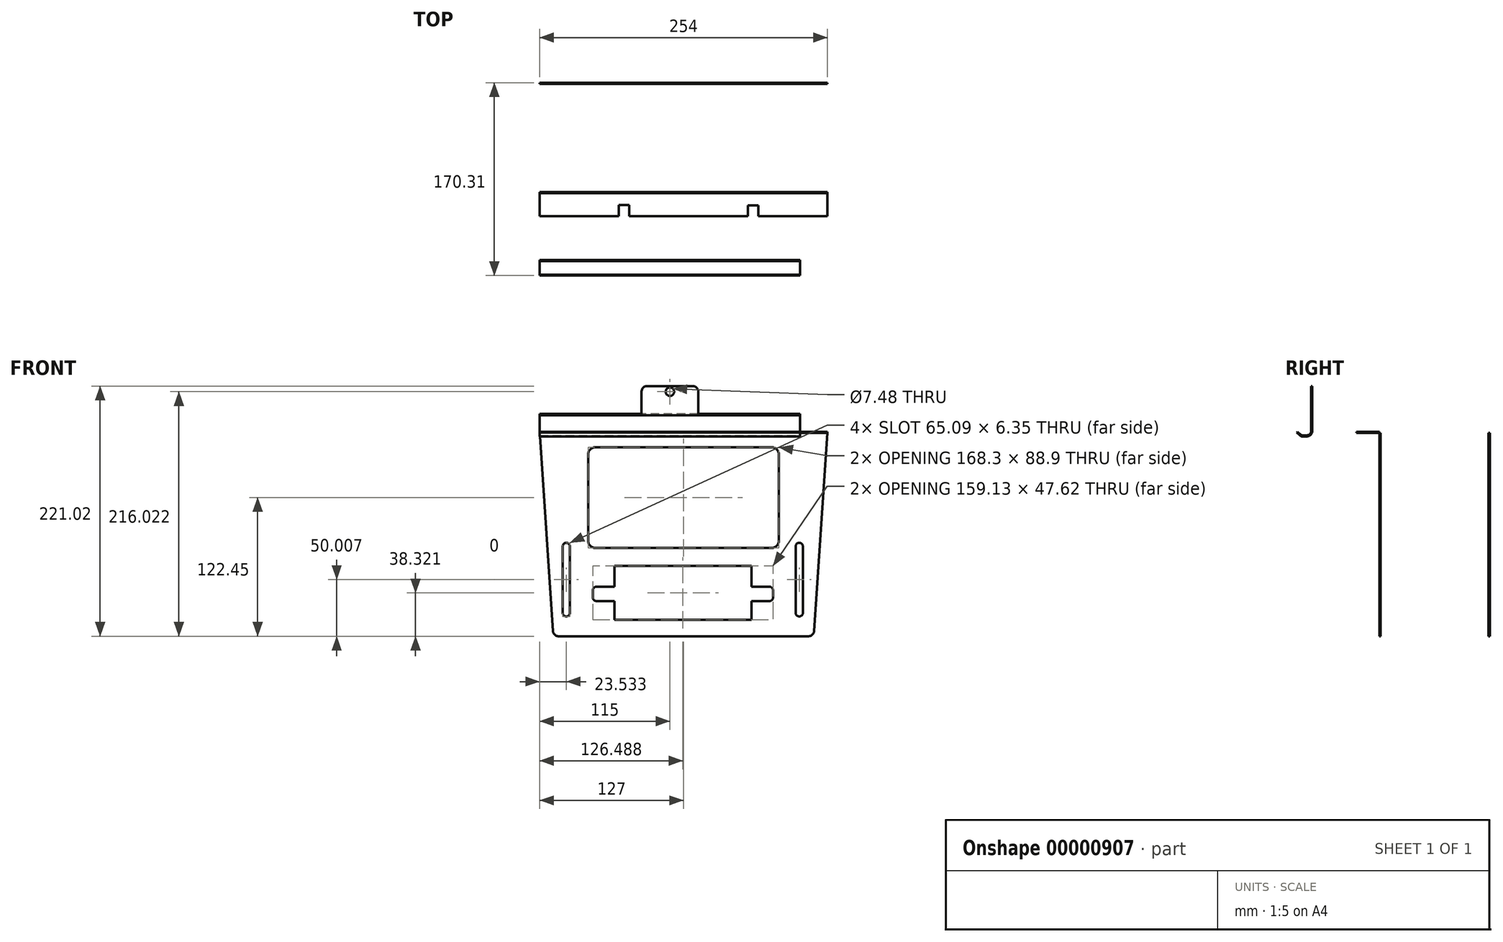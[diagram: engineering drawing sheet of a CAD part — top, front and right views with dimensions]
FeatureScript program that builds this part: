
annotation { "Feature Type Name" : "Feature", "Feature Type Description" : "" }
export const myFeature = defineFeature(function(context is Context, id is Id, definition is map)
    precondition{}
    {
        {
            var Q0;
            Q0=qCreatedBy(makeId("Top.planeOp"),FACE);
            var sketch = newSketch(context, id + "F0", { "sketchPlane" : qUnion([Q0])});
            skLineSegment(sketch, "E0", {"start": v(0, 0) * mm, "end": v(254, 0) * mm});
            skLineSegment(sketch, "E1", {"start": v(254, 0) * mm, "end": v(254, 20.25) * mm});
            skLineSegment(sketch, "E2", {"start": v(254, 20.25) * mm, "end": v(0, 20.25) * mm});
            skLineSegment(sketch, "E3", {"start": v(0, 20.25) * mm, "end": v(0, 0) * mm});
            skLineSegment(sketch, "E4.bottom", {"start": v(70, 20.25) * mm, "end": v(79, 20.25) * mm});
            skLineSegment(sketch, "E4.top", {"start": v(70, 10.6) * mm, "end": v(79, 10.6) * mm});
            skLineSegment(sketch, "E4.left", {"start": v(70, 20.25) * mm, "end": v(70, 10.6) * mm});
            skLineSegment(sketch, "E4.right", {"start": v(79, 20.25) * mm, "end": v(79, 10.6) * mm});
            skLineSegment(sketch, "E5.bottom", {"start": v(184, 20.25) * mm, "end": v(193, 20.25) * mm});
            skLineSegment(sketch, "E5.top", {"start": v(184, 10.9) * mm, "end": v(193, 10.9) * mm});
            skLineSegment(sketch, "E5.left", {"start": v(193, 20.25) * mm, "end": v(193, 10.9) * mm});
            skLineSegment(sketch, "E5.right", {"start": v(184, 20.25) * mm, "end": v(184, 10.9) * mm});
            skSolve(sketch);
        }
        {
            var Q0;
            Q0=qCreatedBy(makeId("Front.planeOp"),FACE);
            var sketch = newSketch(context, id + "F1", { "sketchPlane" : qUnion([Q0])});
            skLineSegment(sketch, "E6", {"start": v(0, 0) * mm, "end": v(11.69, 174.93) * mm});
            skLineSegment(sketch, "E7", {"start": v(16.68, 179.6) * mm, "end": v(237.32, 179.6) * mm});
            skLineSegment(sketch, "E8", {"start": v(242.31, 174.93) * mm, "end": v(254, 0) * mm});
            skLineSegment(sketch, "E9", {"start": v(254, 0) * mm, "end": v(0, 0) * mm});
            skPoint(sketch, "E10.visualSharp", {"position": v(12, 179.6) * mm});
            skArc(sketch, "E10.filletArc", {"start": v(16.68, 179.6) * mm, "mid": v(13.26, 178.25) * mm, "end": v(11.69, 174.93) * mm});
            skPoint(sketch, "E11.visualSharp", {"position": v(242, 179.6) * mm});
            skArc(sketch, "E11.filletArc", {"start": v(242.31, 174.93) * mm, "mid": v(240.74, 178.25) * mm, "end": v(237.32, 179.6) * mm});
            skLineSegment(sketch, "E12", {"start": v(16.68, 179.6) * mm, "end": v(16.68, 199.6) * mm});
            skLineSegment(sketch, "E13", {"start": v(16.68, 199.6) * mm, "end": v(236.05, 199.6) * mm});
            skLineSegment(sketch, "E14", {"start": v(236.05, 199.6) * mm, "end": v(237.32, 179.6) * mm});
            skLineSegment(sketch, "E15.bottom", {"start": v(49.2, 101.6) * mm, "end": v(204.8, 101.6) * mm});
            skLineSegment(sketch, "E15.top", {"start": v(49.2, 12.7) * mm, "end": v(204.8, 12.7) * mm});
            skLineSegment(sketch, "E15.left", {"start": v(42.85, 95.25) * mm, "end": v(42.85, 19.05) * mm});
            skLineSegment(sketch, "E15.right", {"start": v(211.15, 95.25) * mm, "end": v(211.15, 19.05) * mm});
            skPoint(sketch, "E16.visualSharp", {"position": v(42.85, 101.6) * mm});
            skArc(sketch, "E16.filletArc", {"start": v(49.2, 101.6) * mm, "mid": v(44.7, 99.74) * mm, "end": v(42.85, 95.25) * mm});
            skPoint(sketch, "E17.visualSharp", {"position": v(211.15, 101.6) * mm});
            skArc(sketch, "E17.filletArc", {"start": v(211.15, 95.25) * mm, "mid": v(209.3, 99.74) * mm, "end": v(204.8, 101.6) * mm});
            skPoint(sketch, "E18.visualSharp", {"position": v(211.15, 12.7) * mm});
            skArc(sketch, "E18.filletArc", {"start": v(204.8, 12.7) * mm, "mid": v(209.3, 14.56) * mm, "end": v(211.15, 19.05) * mm});
            skPoint(sketch, "E19.visualSharp", {"position": v(42.85, 12.7) * mm});
            skArc(sketch, "E19.filletArc", {"start": v(42.85, 19.05) * mm, "mid": v(44.7, 14.56) * mm, "end": v(49.2, 12.7) * mm});
            skLineSegment(sketch, "E20.bottom", {"start": v(65.97, 165.1) * mm, "end": v(187, 165.1) * mm});
            skLineSegment(sketch, "E20.top", {"start": v(65.97, 117.47) * mm, "end": v(187, 117.47) * mm});
            skLineSegment(sketch, "E21.bottom", {"start": v(23.53, 162.14) * mm, "end": v(23.53, 162.14) * mm});
            skLineSegment(sketch, "E21.top", {"start": v(23.53, 97.05) * mm, "end": v(23.53, 97.05) * mm});
            skLineSegment(sketch, "E21.left", {"start": v(26.7, 158.96) * mm, "end": v(26.7, 100.22) * mm});
            skLineSegment(sketch, "E21.right", {"start": v(20.36, 158.96) * mm, "end": v(20.36, 100.22) * mm});
            skPoint(sketch, "E22.visualSharp", {"position": v(26.7, 162.14) * mm});
            skArc(sketch, "E22.filletArc", {"start": v(26.7, 158.96) * mm, "mid": v(25.78, 161.2) * mm, "end": v(23.53, 162.14) * mm});
            skPoint(sketch, "E23.visualSharp", {"position": v(26.7, 97.05) * mm});
            skArc(sketch, "E23.filletArc", {"start": v(23.53, 97.05) * mm, "mid": v(25.78, 97.98) * mm, "end": v(26.7, 100.22) * mm});
            skPoint(sketch, "E24.visualSharp", {"position": v(20.36, 97.05) * mm});
            skArc(sketch, "E24.filletArc", {"start": v(20.36, 100.22) * mm, "mid": v(21.29, 97.98) * mm, "end": v(23.53, 97.05) * mm});
            skPoint(sketch, "E25.visualSharp", {"position": v(20.36, 162.14) * mm});
            skArc(sketch, "E25.filletArc", {"start": v(23.53, 162.14) * mm, "mid": v(21.29, 161.2) * mm, "end": v(20.36, 158.96) * mm});
            skArc(sketch, "E26.0.MirrorCS", {"start": v(229.2, 97.05) * mm, "mid": v(226.95, 97.98) * mm, "end": v(226.02, 100.22) * mm});
            skArc(sketch, "E26.1.MirrorCS", {"start": v(226.02, 158.96) * mm, "mid": v(226.95, 161.2) * mm, "end": v(229.2, 162.14) * mm});
            skPoint(sketch, "E26.2.MirrorP", {"position": v(232.37, 97.05) * mm});
            skLineSegment(sketch, "E26.3.MirrorCS", {"start": v(226.02, 158.96) * mm, "end": v(226.02, 100.22) * mm});
            skPoint(sketch, "E26.4.MirrorP", {"position": v(226.02, 97.05) * mm});
            skArc(sketch, "E26.5.MirrorCS", {"start": v(229.2, 162.14) * mm, "mid": v(231.44, 161.2) * mm, "end": v(232.37, 158.96) * mm});
            skLineSegment(sketch, "E26.6.MirrorCS", {"start": v(232.37, 158.96) * mm, "end": v(232.37, 100.22) * mm});
            skPoint(sketch, "E26.7.MirrorP", {"position": v(226.02, 162.14) * mm});
            skArc(sketch, "E26.9.MirrorCS", {"start": v(232.37, 100.22) * mm, "mid": v(231.44, 97.98) * mm, "end": v(229.2, 97.05) * mm});
            skPoint(sketch, "E26.10.MirrorP", {"position": v(232.37, 162.14) * mm});
            skLineSegment(sketch, "E27.bottom", {"start": v(65.97, 148.57) * mm, "end": v(50.1, 148.57) * mm});
            skLineSegment(sketch, "E27.top", {"start": v(65.97, 135.87) * mm, "end": v(50.1, 135.87) * mm});
            skLineSegment(sketch, "E27.right", {"start": v(46.92, 145.4) * mm, "end": v(46.92, 139.04) * mm});
            skLineSegment(sketch, "E28", {"start": v(65.97, 165.1) * mm, "end": v(65.97, 148.57) * mm});
            skLineSegment(sketch, "E29", {"start": v(65.97, 135.87) * mm, "end": v(65.97, 117.47) * mm});
            skPoint(sketch, "E30.visualSharp", {"position": v(46.92, 148.57) * mm});
            skArc(sketch, "E30.filletArc", {"start": v(50.1, 148.57) * mm, "mid": v(47.85, 147.64) * mm, "end": v(46.92, 145.4) * mm});
            skPoint(sketch, "E31.visualSharp", {"position": v(46.92, 135.87) * mm});
            skArc(sketch, "E31.filletArc", {"start": v(46.92, 139.04) * mm, "mid": v(47.85, 136.8) * mm, "end": v(50.1, 135.87) * mm});
            skArc(sketch, "E32.0.MirrorCS", {"start": v(202.88, 148.57) * mm, "mid": v(205.12, 147.64) * mm, "end": v(206.05, 145.4) * mm});
            skLineSegment(sketch, "E32.1.MirrorCS", {"start": v(206.05, 145.4) * mm, "end": v(206.05, 139.04) * mm});
            skArc(sketch, "E32.2.MirrorCS", {"start": v(206.05, 139.04) * mm, "mid": v(205.12, 136.8) * mm, "end": v(202.88, 135.87) * mm});
            skPoint(sketch, "E32.3.MirrorP", {"position": v(206.05, 135.87) * mm});
            skPoint(sketch, "E32.4.MirrorP", {"position": v(206.05, 148.57) * mm});
            skLineSegment(sketch, "E33.0.MirrorCS", {"start": v(187, 148.57) * mm, "end": v(202.88, 148.57) * mm});
            skLineSegment(sketch, "E34.0.MirrorCS", {"start": v(187, 135.87) * mm, "end": v(202.88, 135.87) * mm});
            skLineSegment(sketch, "E35", {"start": v(187, 148.57) * mm, "end": v(187, 165.1) * mm});
            skLineSegment(sketch, "E36", {"start": v(187, 135.87) * mm, "end": v(187, 117.47) * mm});
            skSolve(sketch);
        }
        {
            var Q0;
            Q0=makeQuery(id+"F1.imprint","IMPRINT",FACE,{"disambiguationData":[TD([[makeQuery(id+"F1.imprint","IMPRINT",EDGE,{"derivedFrom":sQuery(id+"F1.wireOp",EDGE,"E6")}),-1.0]])]});
            extrude(context, id + "F2", {"entities" : qUnion([Q0]), "depth" : 1 * mm});
        }
        {
            var Q0;
            Q0=makeQuery(id+"F0.imprint","IMPRINT",FACE,{"disambiguationData":[TD([[makeQuery(id+"F0.imprint","IMPRINT",EDGE,{"derivedFrom":sQuery(id+"F0.wireOp",EDGE,"E0")}),1.0]])]});
            extrude(context, id + "F3", {"entities" : qUnion([Q0]), "operationType" : NewBodyOperationType.ADD, "oppositeDirection" : true, "depth" : 1 * mm});
        }
        {
            var Q0;
            Q0=makeQuery(id+"F2.opExtrude","SWEPT_BODY",BODY,{"disambiguationData":[OSD([sQuery(id+"F1.wireOp",EDGE,"E6"),sQuery(id+"F1.wireOp",EDGE,"E7"),sQuery(id+"F1.wireOp",EDGE,"E8"),sQuery(id+"F1.wireOp",EDGE,"E9"),sQuery(id+"F1.wireOp",EDGE,"E10.filletArc"),sQuery(id+"F1.wireOp",EDGE,"E11.filletArc"),sQuery(id+"F1.wireOp",EDGE,"E15.bottom"),sQuery(id+"F1.wireOp",EDGE,"E15.top"),sQuery(id+"F1.wireOp",EDGE,"E15.left"),sQuery(id+"F1.wireOp",EDGE,"E15.right"),sQuery(id+"F1.wireOp",EDGE,"E16.filletArc"),sQuery(id+"F1.wireOp",EDGE,"E17.filletArc"),sQuery(id+"F1.wireOp",EDGE,"E18.filletArc"),sQuery(id+"F1.wireOp",EDGE,"E19.filletArc"),sQuery(id+"F1.wireOp",EDGE,"E20.bottom"),sQuery(id+"F1.wireOp",EDGE,"E20.top"),sQuery(id+"F1.wireOp",EDGE,"E21.left"),sQuery(id+"F1.wireOp",EDGE,"E21.right"),sQuery(id+"F1.wireOp",EDGE,"E22.filletArc"),sQuery(id+"F1.wireOp",EDGE,"E23.filletArc"),sQuery(id+"F1.wireOp",EDGE,"E24.filletArc"),sQuery(id+"F1.wireOp",EDGE,"E25.filletArc"),sQuery(id+"F1.wireOp",EDGE,"E26.0.MirrorCS"),sQuery(id+"F1.wireOp",EDGE,"E26.1.MirrorCS"),sQuery(id+"F1.wireOp",EDGE,"E26.3.MirrorCS"),sQuery(id+"F1.wireOp",EDGE,"E26.5.MirrorCS"),sQuery(id+"F1.wireOp",EDGE,"E26.6.MirrorCS"),sQuery(id+"F1.wireOp",EDGE,"E26.9.MirrorCS"),sQuery(id+"F1.wireOp",EDGE,"E27.bottom"),sQuery(id+"F1.wireOp",EDGE,"E27.top"),sQuery(id+"F1.wireOp",EDGE,"E27.right"),sQuery(id+"F1.wireOp",EDGE,"E28"),sQuery(id+"F1.wireOp",EDGE,"E29"),sQuery(id+"F1.wireOp",EDGE,"E30.filletArc"),sQuery(id+"F1.wireOp",EDGE,"E31.filletArc"),sQuery(id+"F1.wireOp",EDGE,"E32.0.MirrorCS"),sQuery(id+"F1.wireOp",EDGE,"E32.1.MirrorCS"),sQuery(id+"F1.wireOp",EDGE,"E32.2.MirrorCS"),sQuery(id+"F1.wireOp",EDGE,"E33.0.MirrorCS"),sQuery(id+"F1.wireOp",EDGE,"E34.0.MirrorCS"),sQuery(id+"F1.wireOp",EDGE,"E35"),sQuery(id+"F1.wireOp",EDGE,"E36")])]});
            var Q1;
            Q1=makeQuery(id+"F3.opExtrude","SWEPT_BODY",BODY,{"disambiguationData":[OSD([sQuery(id+"F0.wireOp",EDGE,"E0"),sQuery(id+"F0.wireOp",EDGE,"E1"),sQuery(id+"F0.wireOp",EDGE,"E2"),sQuery(id+"F0.wireOp",EDGE,"E3"),sQuery(id+"F0.wireOp",EDGE,"E4.top"),sQuery(id+"F0.wireOp",EDGE,"E4.left"),sQuery(id+"F0.wireOp",EDGE,"E4.right"),sQuery(id+"F0.wireOp",EDGE,"E5.top"),sQuery(id+"F0.wireOp",EDGE,"E5.left"),sQuery(id+"F0.wireOp",EDGE,"E5.right")])]});
            var Q2;
            Q2=makeQuery(id+"F2.opExtrude","CAP_EDGE",EDGE,{"disambiguationData":[OSD([sQuery(id+"F1.wireOp",EDGE,"E9")])],"isStart":false});
            transform(context, id + "F4", {"entities" : qUnion([Q0, Q1]), "transformType" : TransformType.ROTATION, "transformAxis" : qUnion([Q2]), "angle" : 180 * degree, "oppositeX" : false, "oppositeY" : false, "oppositeZ" : false, "makeCopy" : false});
        }
        {
            var Q0;
            Q0=qCreatedBy(makeId("Right.planeOp"),FACE);
            var sketch = newSketch(context, id + "F5", { "sketchPlane" : qUnion([Q0])});
            skLineSegment(sketch, "E37", {"start": v(-74.88, 0.2) * mm, "end": v(-71.14, -3.12) * mm});
            skLineSegment(sketch, "E38", {"start": v(-71.14, -3.12) * mm, "end": v(-61.14, -3.12) * mm});
            skLineSegment(sketch, "E39", {"start": v(-61.14, -3.12) * mm, "end": v(-61.14, 16.88) * mm});
            skLineSegment(sketch, "E40", {"start": v(-74.88, 0.2) * mm, "end": v(-61.14, 16.88) * mm});
            skSolve(sketch);
        }
        {
            var Q0;
            Q0=makeQuery(id+"F5.imprint","IMPRINT",FACE,{"disambiguationData":[TD([[makeQuery(id+"F5.imprint","IMPRINT",EDGE,{"derivedFrom":sQuery(id+"F5.wireOp",EDGE,"E37")}),1.0]])]});
            extrude(context, id + "F6", {"entities" : qUnion([Q0]), "depth" : 230 * mm});
        }
        {
            var Q0;
            Q0=makeQuery(id+"F6.opExtrude","SWEPT_EDGE",EDGE,{"disambiguationData":[OSD([sQuery(id+"F5.wireOp",EDGE,"E37"),sQuery(id+"F5.wireOp",EDGE,"E38")])]});
            fillet(context, id + "F7", {"entities" : qUnion([Q0]), "radius" : 3 * mm, "tangentPropagation" : true, "allowEdgeOverflow" : false});
        }
        {
            var Q0;
            Q0=makeQuery(id+"F6.opExtrude","SWEPT_EDGE",EDGE,{"disambiguationData":[OSD([sQuery(id+"F5.wireOp",EDGE,"E38"),sQuery(id+"F5.wireOp",EDGE,"E39")])]});
            fillet(context, id + "F8", {"entities" : qUnion([Q0]), "radius" : 5 * mm, "tangentPropagation" : true, "allowEdgeOverflow" : false});
        }
        {
            var Q0;
            Q0=makeQuery(id+"F6.opExtrude","SWEPT_FACE",FACE,{"disambiguationData":[OSD([sQuery(id+"F5.wireOp",EDGE,"E40")])]});
            var Q1;
            Q1=makeQuery(id+"F6.opExtrude","CAP_FACE",FACE,{"disambiguationData":[OSD([sQuery(id+"F5.wireOp",EDGE,"E37"),sQuery(id+"F5.wireOp",EDGE,"E38"),sQuery(id+"F5.wireOp",EDGE,"E39"),sQuery(id+"F5.wireOp",EDGE,"E40")])],"isStart":false});
            var Q2;
            Q2=makeQuery(id+"F6.opExtrude","CAP_FACE",FACE,{"disambiguationData":[OSD([sQuery(id+"F5.wireOp",EDGE,"E37"),sQuery(id+"F5.wireOp",EDGE,"E38"),sQuery(id+"F5.wireOp",EDGE,"E39"),sQuery(id+"F5.wireOp",EDGE,"E40")])],"isStart":true});
            shell(context, id + "F9", {"entities" : qUnion([Q0, Q1, Q2]), "thickness" : 1 * mm});
        }
        {
            var Q0;
            Q0=makeQuery(id+"F9.opShell","OFFSET_FACE",FACE,{"disambiguationData":[OSD([sQuery(id+"F5.wireOp",EDGE,"E39")])]});
            var sketch = newSketch(context, id + "F10", { "sketchPlane" : qUnion([Q0])});
            skLineSegment(sketch, "E41", {"start": v(90, 15.67) * mm, "end": v(90, 36.42) * mm});
            skLineSegment(sketch, "E42", {"start": v(95, 41.42) * mm, "end": v(135, 41.42) * mm});
            skLineSegment(sketch, "E43", {"start": v(140, 36.42) * mm, "end": v(140, 15.67) * mm});
            skPoint(sketch, "E44.visualSharp", {"position": v(90, 41.42) * mm});
            skArc(sketch, "E44.filletArc", {"start": v(95, 41.42) * mm, "mid": v(91.46, 39.96) * mm, "end": v(90, 36.42) * mm});
            skPoint(sketch, "E45.visualSharp", {"position": v(140, 41.42) * mm});
            skArc(sketch, "E45.filletArc", {"start": v(140, 36.42) * mm, "mid": v(138.54, 39.96) * mm, "end": v(135, 41.42) * mm});
            skCircle(sketch, "E46", {"center": v(115, 36.42) * mm, "radius": 3.74 * mm});
            skSolve(sketch);
        }
        {
            var Q0;
            {var subQ2=sQuery(id+"F10.wireOp",EDGE,"E41");Q0=makeQuery(id+"F10.imprint","IMPRINT",FACE,{"disambiguationData":[TD([[makeQuery(id+"F10.imprint","IMPRINT",EDGE,{"derivedFrom":subQ2}),-1.0]])]});}
            extrude(context, id + "F11", {"entities" : qUnion([Q0]), "oppositeDirection" : true, "depth" : 1 * mm});
        }
        {
            var Q0;
            Q0=makeQuery(id+"F2.opExtrude","SWEPT_BODY",BODY,{"disambiguationData":[OSD([sQuery(id+"F1.wireOp",EDGE,"E6"),sQuery(id+"F1.wireOp",EDGE,"E7"),sQuery(id+"F1.wireOp",EDGE,"E8"),sQuery(id+"F1.wireOp",EDGE,"E9"),sQuery(id+"F1.wireOp",EDGE,"E10.filletArc"),sQuery(id+"F1.wireOp",EDGE,"E11.filletArc"),sQuery(id+"F1.wireOp",EDGE,"E15.bottom"),sQuery(id+"F1.wireOp",EDGE,"E15.top"),sQuery(id+"F1.wireOp",EDGE,"E15.left"),sQuery(id+"F1.wireOp",EDGE,"E15.right"),sQuery(id+"F1.wireOp",EDGE,"E16.filletArc"),sQuery(id+"F1.wireOp",EDGE,"E17.filletArc"),sQuery(id+"F1.wireOp",EDGE,"E18.filletArc"),sQuery(id+"F1.wireOp",EDGE,"E19.filletArc"),sQuery(id+"F1.wireOp",EDGE,"E20.bottom"),sQuery(id+"F1.wireOp",EDGE,"E20.top"),sQuery(id+"F1.wireOp",EDGE,"E21.left"),sQuery(id+"F1.wireOp",EDGE,"E21.right"),sQuery(id+"F1.wireOp",EDGE,"E22.filletArc"),sQuery(id+"F1.wireOp",EDGE,"E23.filletArc"),sQuery(id+"F1.wireOp",EDGE,"E24.filletArc"),sQuery(id+"F1.wireOp",EDGE,"E25.filletArc"),sQuery(id+"F1.wireOp",EDGE,"E26.0.MirrorCS"),sQuery(id+"F1.wireOp",EDGE,"E26.1.MirrorCS"),sQuery(id+"F1.wireOp",EDGE,"E26.3.MirrorCS"),sQuery(id+"F1.wireOp",EDGE,"E26.5.MirrorCS"),sQuery(id+"F1.wireOp",EDGE,"E26.6.MirrorCS"),sQuery(id+"F1.wireOp",EDGE,"E26.9.MirrorCS"),sQuery(id+"F1.wireOp",EDGE,"E27.bottom"),sQuery(id+"F1.wireOp",EDGE,"E27.top"),sQuery(id+"F1.wireOp",EDGE,"E27.right"),sQuery(id+"F1.wireOp",EDGE,"E28"),sQuery(id+"F1.wireOp",EDGE,"E29"),sQuery(id+"F1.wireOp",EDGE,"E30.filletArc"),sQuery(id+"F1.wireOp",EDGE,"E31.filletArc"),sQuery(id+"F1.wireOp",EDGE,"E32.0.MirrorCS"),sQuery(id+"F1.wireOp",EDGE,"E32.1.MirrorCS"),sQuery(id+"F1.wireOp",EDGE,"E32.2.MirrorCS"),sQuery(id+"F1.wireOp",EDGE,"E33.0.MirrorCS"),sQuery(id+"F1.wireOp",EDGE,"E34.0.MirrorCS"),sQuery(id+"F1.wireOp",EDGE,"E35"),sQuery(id+"F1.wireOp",EDGE,"E36")])]});
            transform(context, id + "F12", {"entities" : qUnion([Q0]), "transformType" : TransformType.COPY});
        }
        {
            var Q0;
            Q0=makeQuery(id+"F2.opExtrude","SWEPT_BODY",BODY,{"disambiguationData":[OSD([sQuery(id+"F1.wireOp",EDGE,"E6"),sQuery(id+"F1.wireOp",EDGE,"E7"),sQuery(id+"F1.wireOp",EDGE,"E8"),sQuery(id+"F1.wireOp",EDGE,"E9"),sQuery(id+"F1.wireOp",EDGE,"E10.filletArc"),sQuery(id+"F1.wireOp",EDGE,"E11.filletArc"),sQuery(id+"F1.wireOp",EDGE,"E15.bottom"),sQuery(id+"F1.wireOp",EDGE,"E15.top"),sQuery(id+"F1.wireOp",EDGE,"E15.left"),sQuery(id+"F1.wireOp",EDGE,"E15.right"),sQuery(id+"F1.wireOp",EDGE,"E16.filletArc"),sQuery(id+"F1.wireOp",EDGE,"E17.filletArc"),sQuery(id+"F1.wireOp",EDGE,"E18.filletArc"),sQuery(id+"F1.wireOp",EDGE,"E19.filletArc"),sQuery(id+"F1.wireOp",EDGE,"E20.bottom"),sQuery(id+"F1.wireOp",EDGE,"E20.top"),sQuery(id+"F1.wireOp",EDGE,"E21.left"),sQuery(id+"F1.wireOp",EDGE,"E21.right"),sQuery(id+"F1.wireOp",EDGE,"E22.filletArc"),sQuery(id+"F1.wireOp",EDGE,"E23.filletArc"),sQuery(id+"F1.wireOp",EDGE,"E24.filletArc"),sQuery(id+"F1.wireOp",EDGE,"E25.filletArc"),sQuery(id+"F1.wireOp",EDGE,"E26.0.MirrorCS"),sQuery(id+"F1.wireOp",EDGE,"E26.1.MirrorCS"),sQuery(id+"F1.wireOp",EDGE,"E26.3.MirrorCS"),sQuery(id+"F1.wireOp",EDGE,"E26.5.MirrorCS"),sQuery(id+"F1.wireOp",EDGE,"E26.6.MirrorCS"),sQuery(id+"F1.wireOp",EDGE,"E26.9.MirrorCS"),sQuery(id+"F1.wireOp",EDGE,"E27.bottom"),sQuery(id+"F1.wireOp",EDGE,"E27.top"),sQuery(id+"F1.wireOp",EDGE,"E27.right"),sQuery(id+"F1.wireOp",EDGE,"E28"),sQuery(id+"F1.wireOp",EDGE,"E29"),sQuery(id+"F1.wireOp",EDGE,"E30.filletArc"),sQuery(id+"F1.wireOp",EDGE,"E31.filletArc"),sQuery(id+"F1.wireOp",EDGE,"E32.0.MirrorCS"),sQuery(id+"F1.wireOp",EDGE,"E32.1.MirrorCS"),sQuery(id+"F1.wireOp",EDGE,"E32.2.MirrorCS"),sQuery(id+"F1.wireOp",EDGE,"E33.0.MirrorCS"),sQuery(id+"F1.wireOp",EDGE,"E34.0.MirrorCS"),sQuery(id+"F1.wireOp",EDGE,"E35"),sQuery(id+"F1.wireOp",EDGE,"E36")])]});
            transform(context, id + "F13", {"entities" : qUnion([Q0]), "transformType" : TransformType.TRANSLATION_3D, "dx" : 0 * mm, "dy" : 96.43 * mm, "dz" : 0 * mm, "makeCopy" : false});
        }
    });
